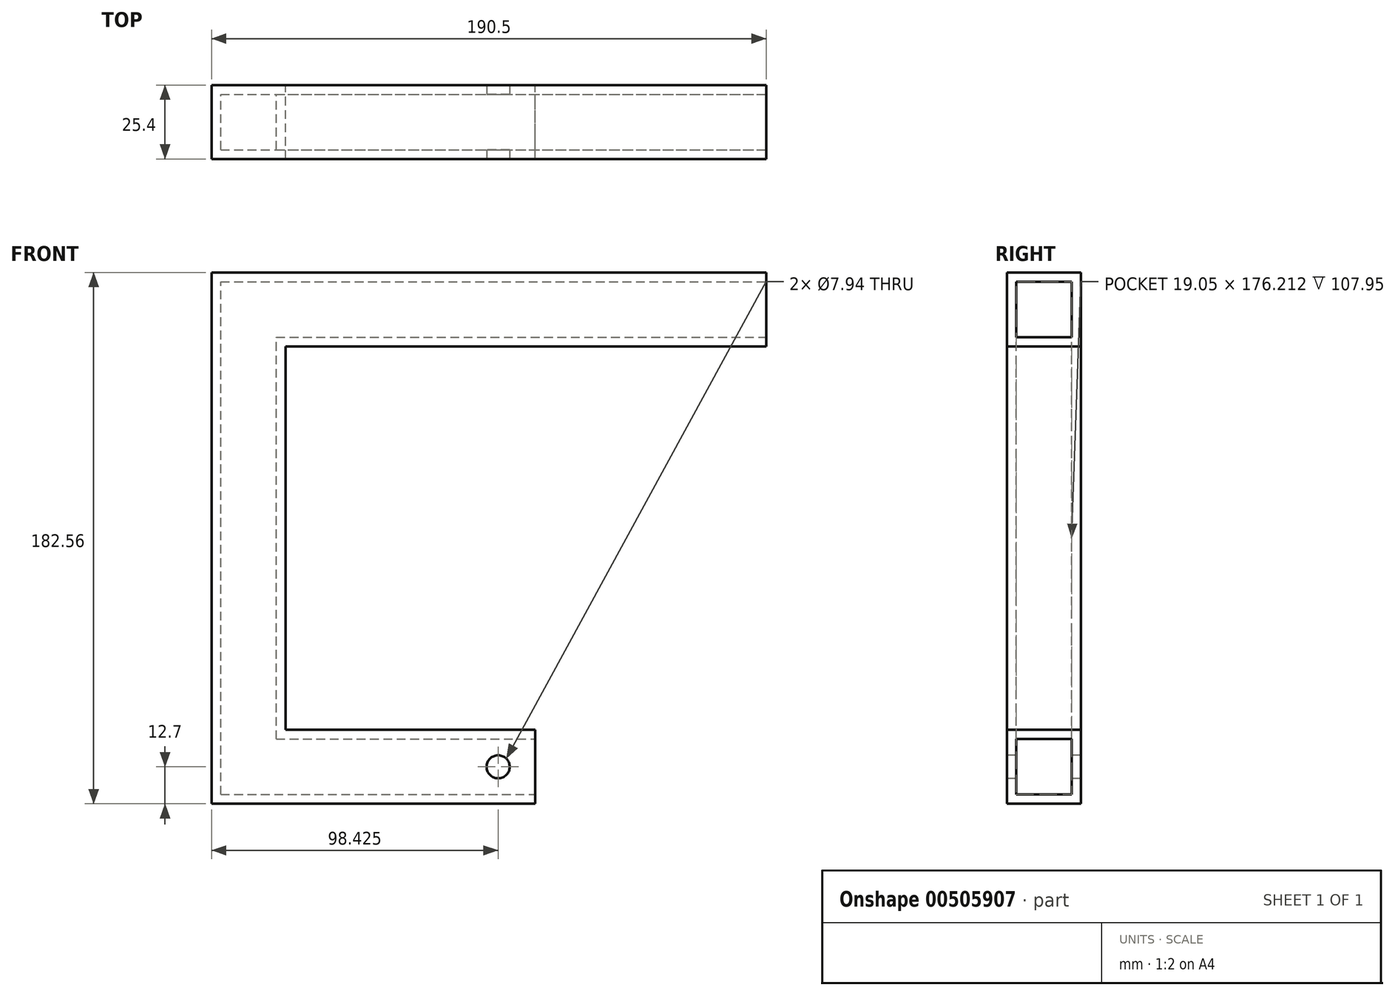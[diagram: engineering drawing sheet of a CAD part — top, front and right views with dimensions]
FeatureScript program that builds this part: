
annotation { "Feature Type Name" : "Feature", "Feature Type Description" : "" }
export const myFeature = defineFeature(function(context is Context, id is Id, definition is map)
    precondition{}
    {
        {
            var Q0;
            Q0=qCreatedBy(makeId("Front.planeOp"),FACE);
            var sketch = newSketch(context, id + "F0", { "sketchPlane" : qUnion([Q0])});
            skLineSegment(sketch, "E0.bottom", {"start": v(0, 0) * mm, "end": v(111.13, 0) * mm});
            skLineSegment(sketch, "E0.left", {"start": v(0, 0) * mm, "end": v(0, 182.56) * mm});
            skLineSegment(sketch, "E0.right", {"start": v(111.13, 0) * mm, "end": v(111.13, 25.4) * mm});
            skLineSegment(sketch, "E1.0", {"start": v(25.4, 25.4) * mm, "end": v(25.4, 157.16) * mm});
            skLineSegment(sketch, "E1.1", {"start": v(25.4, 25.4) * mm, "end": v(111.13, 25.4) * mm});
            skLineSegment(sketch, "E2", {"start": v(25.4, 157.16) * mm, "end": v(190.5, 157.16) * mm});
            skLineSegment(sketch, "E3", {"start": v(0, 182.56) * mm, "end": v(190.5, 182.56) * mm});
            skLineSegment(sketch, "E4", {"start": v(190.5, 157.16) * mm, "end": v(190.5, 182.56) * mm});
            skSolve(sketch);
        }
        {
            var Q0;
            Q0 = qSketchRegion(id + "F0", true);
            extrude(context, id + "F1", {"entities" : qUnion([Q0]), "depth" : 25.4 * mm});
        }
        {
            var Q0;
            Q0=makeQuery(id+"F1.opExtrude","SWEPT_FACE",FACE,{"disambiguationData":[OSD([sQuery(id+"F0.wireOp",EDGE,"E4")])]});
            var Q1;
            Q1=makeQuery(id+"F1.opExtrude","SWEPT_FACE",FACE,{"disambiguationData":[OSD([sQuery(id+"F0.wireOp",EDGE,"E0.right")])]});
            shell(context, id + "F2", {"entities" : qUnion([Q0, Q1]), "thickness" : 3.17 * mm});
        }
        {
            var Q0;
            Q0=makeQuery(id+"F1.opExtrude","CAP_FACE",FACE,{"disambiguationData":[OSD([sQuery(id+"F0.wireOp",EDGE,"E0.bottom"),sQuery(id+"F0.wireOp",EDGE,"E0.top"),sQuery(id+"F0.wireOp",EDGE,"E0.left"),sQuery(id+"F0.wireOp",EDGE,"E0.right"),sQuery(id+"F0.wireOp",EDGE,"E1.0"),sQuery(id+"F0.wireOp",EDGE,"E1.1")])],"isStart":false});
            var sketch = newSketch(context, id + "F3", { "sketchPlane" : qUnion([Q0])});
            skLineSegment(sketch, "E5.0", {"start": v(111.13, 0) * mm, "end": v(111.13, 25.4) * mm, "construction": true});
            skLineSegment(sketch, "E6", {"start": v(111.13, 12.7) * mm, "end": v(-24.74, 12.7) * mm, "construction": true});
            skCircle(sketch, "E7", {"center": v(98.43, 12.7) * mm, "radius": 3.97 * mm});
            skSolve(sketch);
        }
        {
            var Q0;
            Q0 = qSketchRegion(id + "F3", true);
            extrude(context, id + "F4", {"entities" : qUnion([Q0]), "operationType" : NewBodyOperationType.REMOVE, "oppositeDirection" : true, "depth" : 25.4 * mm});
        }
    });
